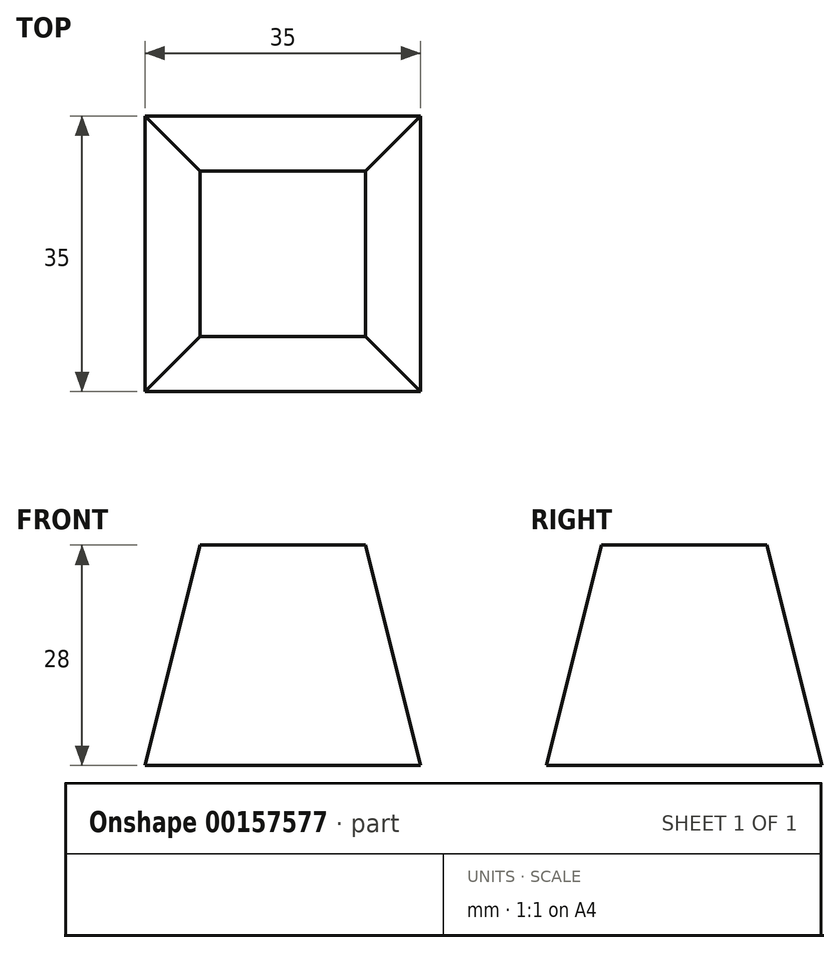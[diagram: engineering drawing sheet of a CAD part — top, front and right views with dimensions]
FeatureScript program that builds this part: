
annotation { "Feature Type Name" : "Feature", "Feature Type Description" : "" }
export const myFeature = defineFeature(function(context is Context, id is Id, definition is map)
    precondition{}
    {
        {
            var Q0;
            Q0=qCreatedBy(makeId("Top.planeOp"),FACE);
            var sketch = newSketch(context, id + "F0", { "sketchPlane" : qUnion([Q0])});
            skLineSegment(sketch, "E0.bottom", {"start": v(10.5, 10.5) * mm, "end": v(-10.5, 10.5) * mm});
            skLineSegment(sketch, "E0.top", {"start": v(10.5, -10.5) * mm, "end": v(-10.5, -10.5) * mm});
            skLineSegment(sketch, "E0.left", {"start": v(10.5, 10.5) * mm, "end": v(10.5, -10.5) * mm});
            skLineSegment(sketch, "E0.right", {"start": v(-10.5, 10.5) * mm, "end": v(-10.5, -10.5) * mm});
            skPoint(sketch, "E0.middle", {"position": v(0, 0) * mm});
            skSolve(sketch);
        }
        {
            var Q0;
            Q0=qCreatedBy(makeId("Top.planeOp"),FACE);
            cPlane(context, id + "F1", {"entities" : qUnion([Q0]), "cplaneType" : CPlaneType.OFFSET, "offset" : 28 * mm, "oppositeDirection" : true, "width" : 150 * mm, "height" : 150 * mm});
        }
        {
            var Q0;
            Q0=qCreatedBy(id+"F1.planeOp",FACE);
            var sketch = newSketch(context, id + "F2", { "sketchPlane" : qUnion([Q0])});
            skLineSegment(sketch, "E1.bottom", {"start": v(17.5, 17.5) * mm, "end": v(-17.5, 17.5) * mm});
            skLineSegment(sketch, "E1.top", {"start": v(17.5, -17.5) * mm, "end": v(-17.5, -17.5) * mm});
            skLineSegment(sketch, "E1.left", {"start": v(17.5, 17.5) * mm, "end": v(17.5, -17.5) * mm});
            skLineSegment(sketch, "E1.right", {"start": v(-17.5, 17.5) * mm, "end": v(-17.5, -17.5) * mm});
            skPoint(sketch, "E1.middle", {"position": v(0, 0) * mm});
            skSolve(sketch);
        }
        {
            var Q0;
            Q0 = qSketchRegion(id + "F0", true);
            var Q1;
            Q1 = qSketchRegion(id + "F2", true);
            loft(context, id + "F3", {"sheetProfilesArray" : [{ "sheetProfileEntities" : qUnion([Q0]) }, { "sheetProfileEntities" : qUnion([Q1]) }]});
        }
    });
